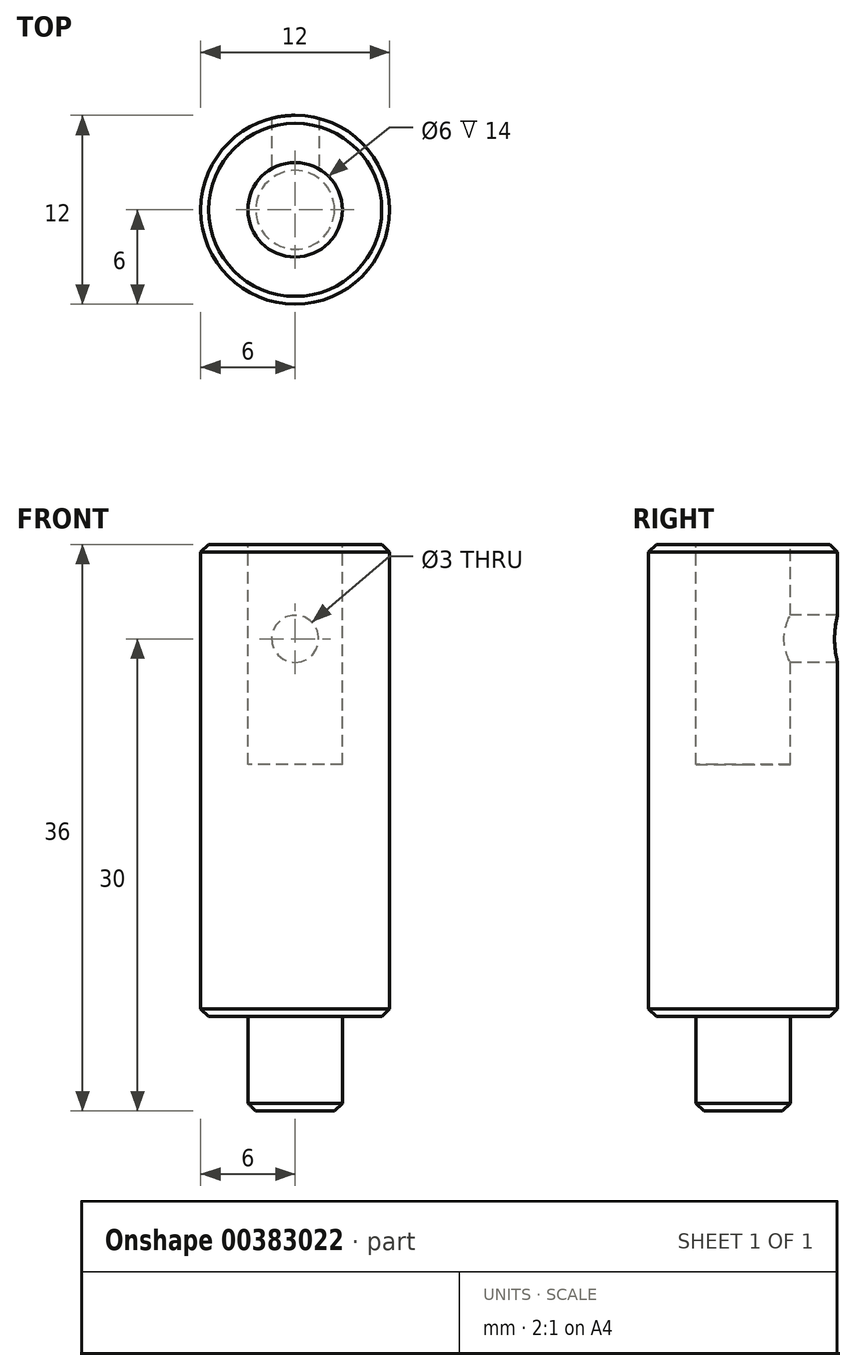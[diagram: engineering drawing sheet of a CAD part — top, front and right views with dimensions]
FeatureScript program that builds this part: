
annotation { "Feature Type Name" : "Feature", "Feature Type Description" : "" }
export const myFeature = defineFeature(function(context is Context, id is Id, definition is map)
    precondition{}
    {
        {
            var Q0;
            Q0=qCreatedBy(makeId("Top.planeOp"),FACE);
            var sketch = newSketch(context, id + "F0", { "sketchPlane" : qUnion([Q0])});
            skCircle(sketch, "E0", {"center": v(0, 0) * mm, "radius": 6 * mm});
            skSolve(sketch);
        }
        {
            var Q0;
            Q0=qSketchRegion(id+"F0",true);
            extrude(context, id + "F1", {"entities" : qUnion([Q0]), "depth" : 30 * mm, "offsetDistance" : 25 * mm});
        }
        {
            var Q0;
            Q0=makeQuery(id+"F1.opExtrude","CAP_FACE",FACE,{"disambiguationData":[OSD([sQuery(id+"F0.wireOp",EDGE,"E0")])],"isStart":true});
            var sketch = newSketch(context, id + "F2", { "sketchPlane" : qUnion([Q0])});
            skCircle(sketch, "E1", {"center": v(0, 0) * mm, "radius": 3 * mm});
            skSolve(sketch);
        }
        {
            var Q0;
            Q0=qSketchRegion(id+"F2",true);
            extrude(context, id + "F3", {"entities" : qUnion([Q0]), "operationType" : NewBodyOperationType.ADD, "depth" : 6 * mm, "offsetDistance" : 25 * mm});
        }
        {
            var Q0;
            Q0=makeQuery(id+"F1.opExtrude","CAP_FACE",FACE,{"disambiguationData":[OSD([sQuery(id+"F0.wireOp",EDGE,"E0")])],"isStart":false});
            var sketch = newSketch(context, id + "F4", { "sketchPlane" : qUnion([Q0])});
            skCircle(sketch, "E2", {"center": v(0, 0) * mm, "radius": 3 * mm});
            skSolve(sketch);
        }
        {
            var Q0;
            Q0=qSketchRegion(id+"F4",true);
            extrude(context, id + "F5", {"entities" : qUnion([Q0]), "operationType" : NewBodyOperationType.REMOVE, "oppositeDirection" : true, "depth" : 14 * mm, "offsetDistance" : 25 * mm});
        }
        {
            var Q0;
            Q0=qCreatedBy(makeId("Front.planeOp"),FACE);
            var sketch = newSketch(context, id + "F6", { "sketchPlane" : qUnion([Q0])});
            skCircle(sketch, "E3", {"center": v(0, 24) * mm, "radius": 1.5 * mm});
            skSolve(sketch);
        }
        {
            var Q0;
            Q0=qSketchRegion(id+"F6",true);
            extrude(context, id + "F7", {"entities" : qUnion([Q0]), "operationType" : NewBodyOperationType.REMOVE, "oppositeDirection" : true, "depth" : 25 * mm, "offsetDistance" : 25 * mm});
        }
        {
            var Q0;
            Q0=makeQuery(id+"F1.opExtrude","CAP_EDGE",EDGE,{"disambiguationData":[OSD([sQuery(id+"F0.wireOp",EDGE,"E0")])],"isStart":true});
            chamfer(context, id + "F8", {"entities" : qUnion([Q0]), "width" : 0.5 * mm, "tangentPropagation" : true});
        }
        {
            var Q0;
            Q0=makeQuery(id+"F3.opExtrude","CAP_EDGE",EDGE,{"disambiguationData":[OSD([sQuery(id+"F2.wireOp",EDGE,"E1")])],"isStart":false});
            chamfer(context, id + "F9", {"entities" : qUnion([Q0]), "width" : 0.5 * mm, "tangentPropagation" : true});
        }
        {
            var Q0;
            Q0=makeQuery(id+"F5.boolean.opBoolean","COPY",EDGE,{"derivedFrom":makeQuery(id+"F5.opExtrude","CAP_EDGE",EDGE,{"disambiguationData":[OSD([sQuery(id+"F4.wireOp",EDGE,"E2")])],"isStart":true})});
            var Q1;
            Q1=makeQuery(id+"F1.opExtrude","CAP_EDGE",EDGE,{"disambiguationData":[OSD([sQuery(id+"F0.wireOp",EDGE,"E0")])],"isStart":false});
            chamfer(context, id + "F10", {"entities" : qUnion([Q0, Q1]), "width" : 0.5 * mm, "tangentPropagation" : true});
        }
    });
